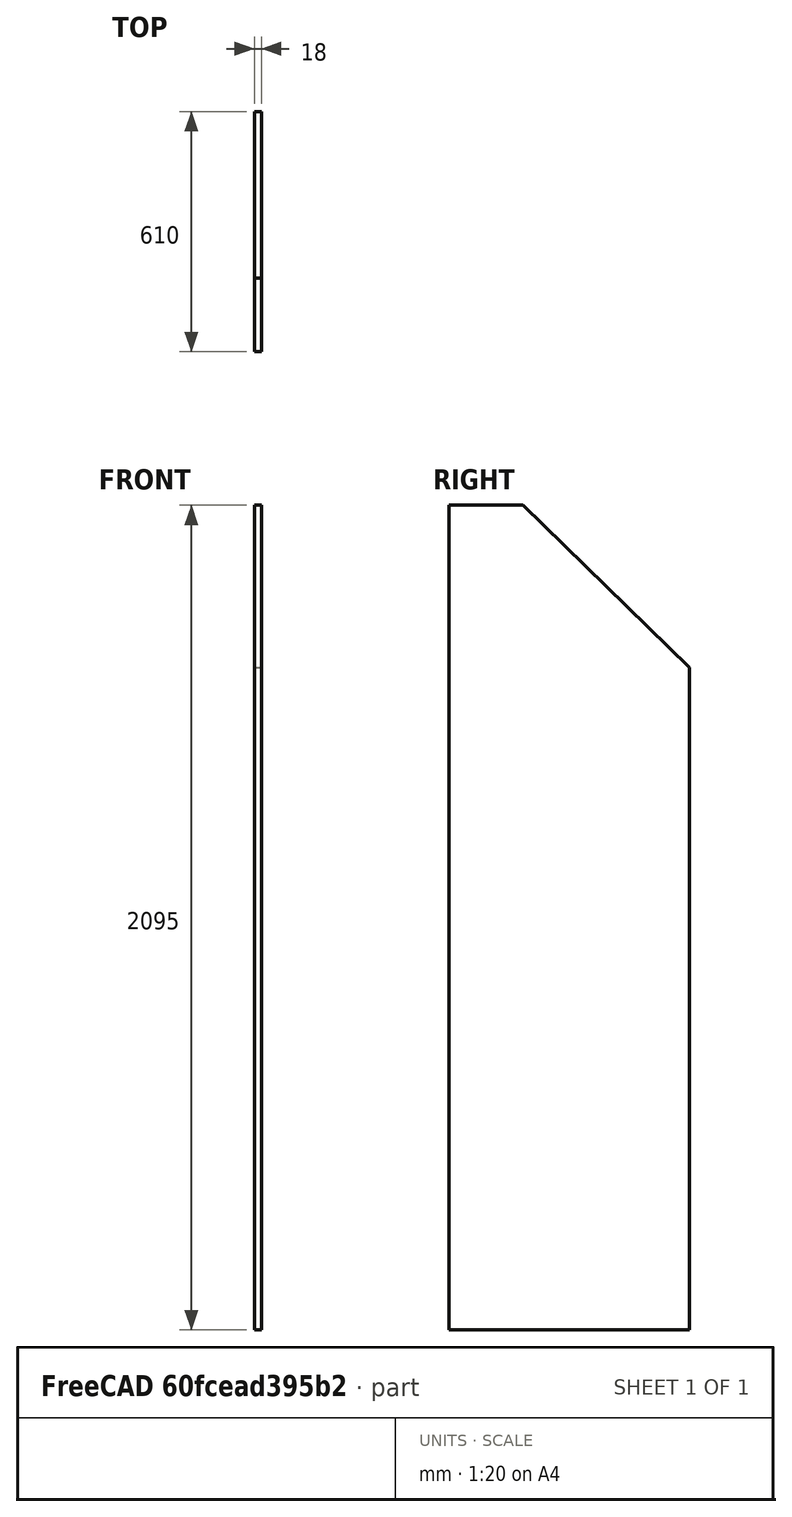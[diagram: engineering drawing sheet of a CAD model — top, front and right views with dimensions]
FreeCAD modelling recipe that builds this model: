
FCSTD DOCUMENT  (FreeCAD 0.17R10980 (Git))
Label: fridge_box_door
License: All rights reserved
LicenseURL: http://en.wikipedia.org/wiki/All_rights_reserved
objects: Part::Part2DObjectPython×1, Part::Extrusion×1, Part::FeaturePython×1
note: 3 computed .brp shape members not serialized (recipe doc carries the construction recipe); baked Part::Feature solids carry a one-line shape summary decoded from their .brp

FEATURE [Part::Part2DObjectPython] DWire008  # Draft 2D object (typed FeaturePython)
  ChamferSize = 0
  Closed = true
  End = (1490,-375,5)
  FilletRadius = 0
  Length = 5165.44
  MakeFace = true
  Points = (5) [(1490,-375,1687.47),(1912.59,-375,2100),(2100,-375,2100),(2100,-375,5),(1490,-375,5)]
  Start = (1490,-375,1687.47)
  Subdivisions = 0
FEATURE [Part::Extrusion] Extrude009
  Base = -> DWire008
  Dir = (0,1,0)
  DirMode = 0
  FaceMakerClass = Part::FaceMakerBullseye
  LengthFwd = 18
  LengthRev = 0
  Solid = false
  Symmetric = false
FEATURE [Part::FeaturePython] Panel009  label="door"  # WARN: FeaturePython — macro-defined, semantics opaque (R4)
  Area = 0
  Base = -> Extrude009
  FaceMaker = 0
  HorizontalArea = 0
  Length = 0
  MoveWithHost = false
  Normal = (0,0,0)
  PerimeterLength = 0
  Placement = pos=(1865,1133,0) rot=(0,0,-1;1.5708rad)
  Role = 0
  Sheets = 1
  Thickness = 10
  VerticalArea = 0
  WaveDirection = 0
  WaveHeight = 0
  WaveLength = 0
  WaveType = 0
  Width = 0
